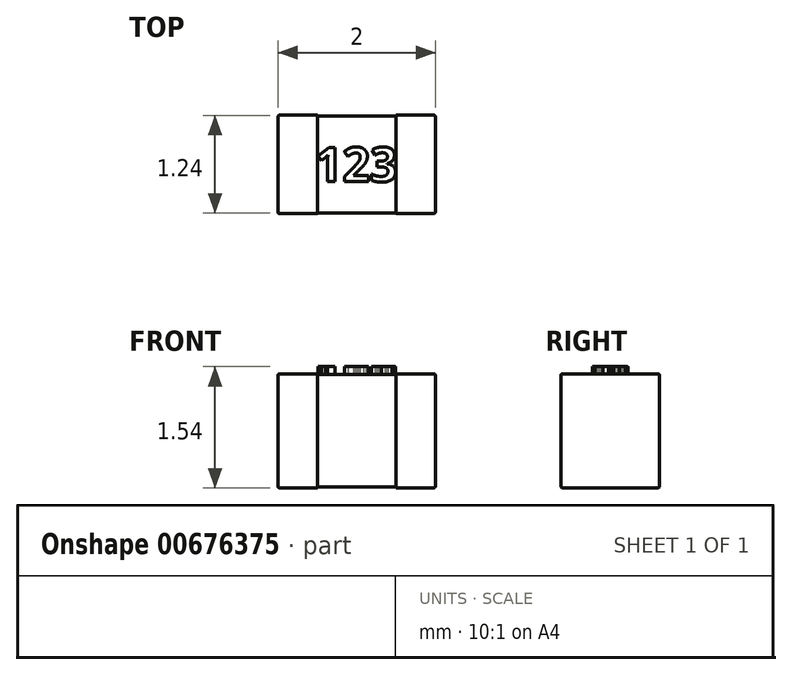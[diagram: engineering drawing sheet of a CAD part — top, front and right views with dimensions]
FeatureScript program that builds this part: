
annotation { "Feature Type Name" : "Feature", "Feature Type Description" : "" }
export const myFeature = defineFeature(function(context is Context, id is Id, definition is map)
    precondition{}
    {
        {
            assignVariable(context, id + "F0", {"name" : "Package", "anyValue" : 2});
        }
        {
            assignVariable(context, id + "F1", {"name" : "T", "anyValue" : [0.6, 0.92, 1.45, 1.7, 1.7, 1.7][getVariable(context, 'Package')]});
        }
        {
            assignVariable(context, id + "F2", {"name" : "R", "anyValue" : [0.02, 0.02, 0.02, 0.02, 0.02, 0.02][getVariable(context, 'Package')]});
        }
        {
            var Q0;
            Q0=qCreatedBy(makeId("Top.planeOp"),FACE);
            var sketch = newSketch(context, id + "F3", { "sketchPlane" : qUnion([Q0])});
            skPoint(sketch, "E0.middle", {"position": v(0, 0) * mm});
            skLineSegment(sketch, "E1.bottom", {"start": v(-1, 0.62) * mm, "end": v(-0.5, 0.62) * mm});
            skLineSegment(sketch, "E1.top", {"start": v(-1, -0.63) * mm, "end": v(-0.5, -0.63) * mm});
            skLineSegment(sketch, "E1.left", {"start": v(-1, 0.62) * mm, "end": v(-1, -0.63) * mm});
            skLineSegment(sketch, "E1.right", {"start": v(-0.5, 0.62) * mm, "end": v(-0.5, -0.63) * mm});
            skPoint(sketch, "E2", {"position": v(-0.5, 0) * mm});
            skLineSegment(sketch, "E3.MirrorCS", {"start": v(1, 0.62) * mm, "end": v(1, -0.63) * mm});
            skLineSegment(sketch, "E4.MirrorCS", {"start": v(0.5, 0.62) * mm, "end": v(0.5, -0.63) * mm});
            skLineSegment(sketch, "E5.MirrorCS", {"start": v(1, -0.63) * mm, "end": v(0.5, -0.63) * mm});
            skLineSegment(sketch, "E6.MirrorCS", {"start": v(1, 0.62) * mm, "end": v(0.5, 0.62) * mm});
            skPoint(sketch, "E7.MirrorP", {"position": v(0.5, 0) * mm});
            skSolve(sketch);
        }
        {
            var Q0;
            Q0=makeQuery(id+"F3.imprint","IMPRINT",FACE,{"disambiguationData":[TD([[makeQuery(id+"F3.imprint","IMPRINT",EDGE,{"derivedFrom":sQuery(id+"F3.wireOp",EDGE,"E1.bottom")}),-1.0]])]});
            var Q1;
            Q1=makeQuery(id+"F3.imprint","IMPRINT",FACE,{"disambiguationData":[TD([[makeQuery(id+"F3.imprint","IMPRINT",EDGE,{"derivedFrom":sQuery(id+"F3.wireOp",EDGE,"E3.MirrorCS")}),-1.0]])]});
            extrude(context, id + "F4", {"entities" : qUnion([Q0, Q1]), "depth" : (getVariable(context, 'T')) * mm, "offsetDistance" : 25 * mm});
        }
        {
            var Q0;
            Q0=makeQuery(id+"F4.opExtrude","SWEPT_FACE",FACE,{"disambiguationData":[OSD([sQuery(id+"F3.wireOp",EDGE,"E1.left")])]});
            var Q1;
            Q1=makeQuery(id+"F4.opExtrude","CAP_EDGE",EDGE,{"disambiguationData":[OSD([sQuery(id+"F3.wireOp",EDGE,"E1.top")])],"isStart":true});
            var Q2;
            Q2=makeQuery(id+"F4.opExtrude","CAP_EDGE",EDGE,{"disambiguationData":[OSD([sQuery(id+"F3.wireOp",EDGE,"E1.top")])],"isStart":false});
            var Q3;
            Q3=makeQuery(id+"F4.opExtrude","CAP_EDGE",EDGE,{"disambiguationData":[OSD([sQuery(id+"F3.wireOp",EDGE,"E1.bottom")])],"isStart":false});
            var Q4;
            Q4=makeQuery(id+"F4.opExtrude","CAP_EDGE",EDGE,{"disambiguationData":[OSD([sQuery(id+"F3.wireOp",EDGE,"E1.bottom")])],"isStart":true});
            var Q5;
            Q5=makeQuery(id+"F4.opExtrude","SWEPT_FACE",FACE,{"disambiguationData":[OSD([sQuery(id+"F3.wireOp",EDGE,"E3.MirrorCS")])]});
            var Q6;
            Q6=makeQuery(id+"F4.opExtrude","CAP_EDGE",EDGE,{"disambiguationData":[OSD([sQuery(id+"F3.wireOp",EDGE,"E5.MirrorCS")])],"isStart":false});
            var Q7;
            Q7=makeQuery(id+"F4.opExtrude","CAP_EDGE",EDGE,{"disambiguationData":[OSD([sQuery(id+"F3.wireOp",EDGE,"E5.MirrorCS")])],"isStart":true});
            var Q8;
            Q8=makeQuery(id+"F4.opExtrude","CAP_EDGE",EDGE,{"disambiguationData":[OSD([sQuery(id+"F3.wireOp",EDGE,"E6.MirrorCS")])],"isStart":true});
            var Q9;
            Q9=makeQuery(id+"F4.opExtrude","CAP_EDGE",EDGE,{"disambiguationData":[OSD([sQuery(id+"F3.wireOp",EDGE,"E6.MirrorCS")])],"isStart":false});
            fillet(context, id + "F5", {"entities" : qUnion([Q0, Q1, Q2, Q3, Q4, Q5, Q6, Q7, Q8, Q9]), "radius" : (getVariable(context, 'R')) * mm, "tangentPropagation" : true, "allowEdgeOverflow" : false});
        }
        {
            var Q0;
            Q0=makeQuery(id+"F4.opExtrude","SWEPT_FACE",FACE,{"disambiguationData":[OSD([sQuery(id+"F3.wireOp",EDGE,"E1.right")])]});
            var sketch = newSketch(context, id + "F6", { "sketchPlane" : qUnion([Q0])});
            skLineSegment(sketch, "E8", {"start": v(0, 1.45) * mm, "end": v(0, 0) * mm, "construction": true});
            skLineSegment(sketch, "E9.bottom", {"start": v(0.61, 1.44) * mm, "end": v(-0.62, 1.44) * mm});
            skLineSegment(sketch, "E9.top", {"start": v(0.61, 0.01) * mm, "end": v(-0.62, 0) * mm});
            skLineSegment(sketch, "E9.left", {"start": v(0.61, 1.44) * mm, "end": v(0.61, 0) * mm});
            skLineSegment(sketch, "E9.right", {"start": v(-0.62, 1.44) * mm, "end": v(-0.62, 0) * mm});
            skPoint(sketch, "E9.middle", {"position": v(0, 0.72) * mm});
            skSolve(sketch);
        }
        {
            var Q0;
            Q0 = qSketchRegion(id + "F6", true);
            extrude(context, id + "F7", {"entities" : qUnion([Q0]), "endBound" : BoundingType.UP_TO_NEXT, "depth" : 25 * mm, "offsetDistance" : 25 * mm});
        }
        {
            var Q0;
            Q0=makeQuery(id+"F7.opExtrude","SWEPT_FACE",FACE,{"disambiguationData":[OSD([sQuery(id+"F6.wireOp",EDGE,"E9.bottom")])]});
            var sketch = newSketch(context, id + "F8", { "sketchPlane" : qUnion([Q0])});
            skText(sketch, "E10", { "text": "123", "fontName": "OpenSans-Bold.ttf"});
            skPoint(sketch, "E11", {"position": v(0.33, 0) * mm});
            const initialGuessF8  = {"E10": [-0.00053, -0.00022, 1, 0, 0.00044]};
            skSetInitialGuess(sketch, initialGuessF8);
            skSolve(sketch);
        }
        {
            var Q0;
            Q0 = qSketchRegion(id + "F8", true);
            extrude(context, id + "F9", {"entities" : qUnion([Q0]), "depth" : .1 * mm, "offsetDistance" : 25 * mm});
        }
    });
